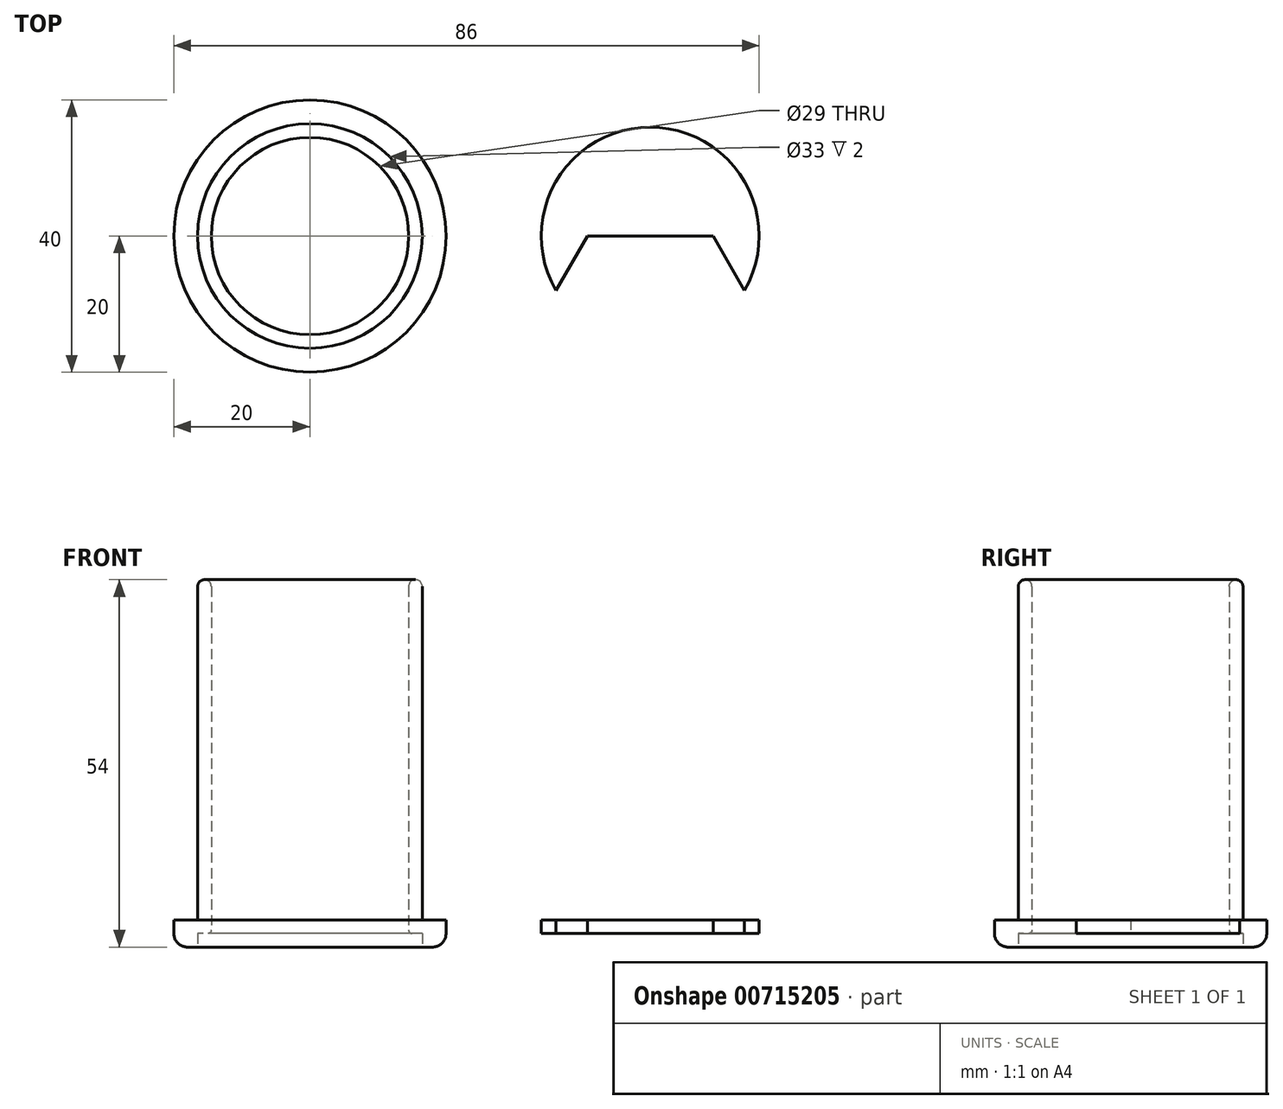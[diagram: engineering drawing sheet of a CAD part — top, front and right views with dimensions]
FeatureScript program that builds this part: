
annotation { "Feature Type Name" : "Feature", "Feature Type Description" : "" }
export const myFeature = defineFeature(function(context is Context, id is Id, definition is map)
    precondition{}
    {
        {
            var Q0;
            Q0=qCreatedBy(makeId("Top.planeOp"),FACE);
            var sketch = newSketch(context, id + "F0", { "sketchPlane" : qUnion([Q0])});
            skCircle(sketch, "E0", {"center": v(0, 0) * mm, "radius": 20 * mm});
            skCircle(sketch, "E1", {"center": v(0, 0) * mm, "radius": 16.5 * mm});
            skCircle(sketch, "E2", {"center": v(0, 0) * mm, "radius": 14.5 * mm});
            skCircle(sketch, "E3", {"center": v(50, 0) * mm, "radius": 16 * mm});
            skCircle(sketch, "E4.cCircle", {"center": v(50, -16) * mm, "radius": 16 * mm, "construction": true});
            skLineSegment(sketch, "E4.0", {"start": v(40.76, 0) * mm, "end": v(59.24, 0) * mm});
            skLineSegment(sketch, "E4.1", {"start": v(59.24, 0) * mm, "end": v(68.48, -16) * mm});
            skLineSegment(sketch, "E4.2", {"start": v(68.48, -16) * mm, "end": v(59.24, -32) * mm});
            skLineSegment(sketch, "E4.3", {"start": v(59.24, -32) * mm, "end": v(40.76, -32) * mm});
            skLineSegment(sketch, "E4.4", {"start": v(40.76, -32) * mm, "end": v(31.52, -16) * mm});
            skLineSegment(sketch, "E4.5", {"start": v(31.52, -16) * mm, "end": v(40.76, 0) * mm});
            skSolve(sketch);
        }
        {
            var Q0;
            Q0=makeQuery(id+"F0.imprint","IMPRINT",FACE,{"disambiguationData":[TD([[makeQuery(id+"F0.imprint","IMPRINT",EDGE,{"derivedFrom":sQuery(id+"F0.wireOp",EDGE,"E1")}),1.0]])]});
            extrude(context, id + "F1", {"entities" : qUnion([Q0]), "depth" : 52 * mm, "offsetDistance" : 25 * mm});
        }
        {
            var Q0;
            Q0=makeQuery(id+"F0.imprint","IMPRINT",FACE,{"disambiguationData":[TD([[makeQuery(id+"F0.imprint","IMPRINT",EDGE,{"derivedFrom":sQuery(id+"F0.wireOp",EDGE,"E0")}),1.0]])]});
            extrude(context, id + "F2", {"entities" : qUnion([Q0]), "operationType" : NewBodyOperationType.ADD, "depth" : 2 * mm, "offsetDistance" : 25 * mm, "hasSecondDirection" : true, "secondDirectionOppositeDirection" : true, "secondDirectionDepth" : 2 * mm});
        }
        {
            var Q0;
            Q0=makeQuery(id+"F2.opExtrude","CAP_EDGE",EDGE,{"disambiguationData":[OSD([sQuery(id+"F0.wireOp",EDGE,"E0")])],"isStart":true});
            fillet(context, id + "F3", {"entities" : qUnion([Q0]), "radius" : 2 * mm, "tangentPropagation" : true, "allowEdgeOverflow" : false});
        }
        {
            var Q0;
            Q0=makeQuery(id+"F1.opExtrude","CAP_FACE",FACE,{"disambiguationData":[OSD([sQuery(id+"F0.wireOp",EDGE,"E1"),sQuery(id+"F0.wireOp",EDGE,"E2")])],"isStart":false});
            fillet(context, id + "F4", {"entities" : qUnion([Q0]), "radius" : 1 * mm, "tangentPropagation" : true, "allowEdgeOverflow" : false});
        }
        {
            var Q0;
            {var subQ5=sQuery(id+"F0.wireOp",EDGE,"E4.0");Q0=makeQuery(id+"F0.imprint","IMPRINT",FACE,{"disambiguationData":[TD([[makeQuery(id+"F0.imprint","IMPRINT",EDGE,{"derivedFrom":subQ5}),1.0]])]});}
            extrude(context, id + "F5", {"entities" : qUnion([Q0]), "depth" : 2 * mm, "offsetDistance" : 25 * mm});
        }
        {
            var Q0;
            Q0=makeQuery(id+"F1.opExtrude","CAP_EDGE",EDGE,{"disambiguationData":[OSD([sQuery(id+"F0.wireOp",EDGE,"E2")])],"isStart":true});
            fillet(context, id + "F6", {"entities" : qUnion([Q0]), "radius" : 0.5 * mm, "tangentPropagation" : true, "allowEdgeOverflow" : false});
        }
    });
